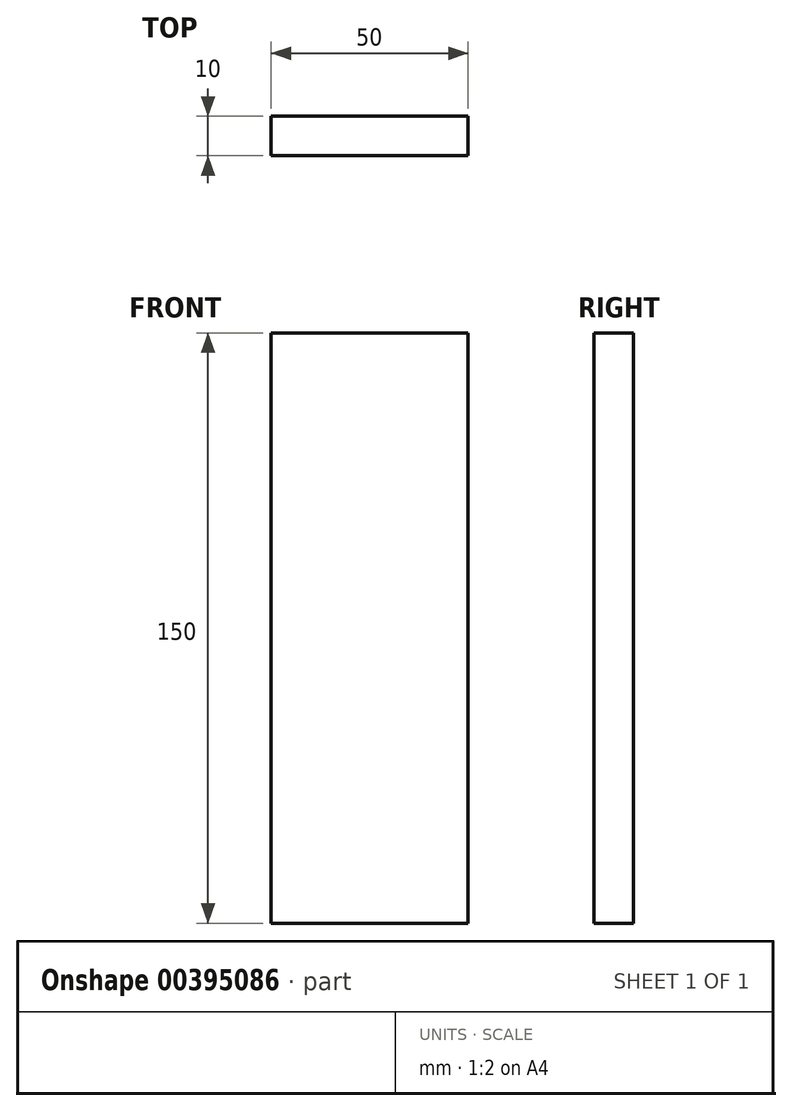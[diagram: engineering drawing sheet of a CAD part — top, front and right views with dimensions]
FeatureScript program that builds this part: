
annotation { "Feature Type Name" : "Feature", "Feature Type Description" : "" }
export const myFeature = defineFeature(function(context is Context, id is Id, definition is map)
    precondition{}
    {
        {
            var Q0;
            Q0=qCreatedBy(makeId("Front.planeOp"),FACE);
            var sketch = newSketch(context, id + "F0", { "sketchPlane" : qUnion([Q0])});
            skLineSegment(sketch, "E0.bottom", {"start": v(-25, -75) * mm, "end": v(25, -75) * mm});
            skLineSegment(sketch, "E0.top", {"start": v(-25, 75) * mm, "end": v(25, 75) * mm});
            skLineSegment(sketch, "E0.left", {"start": v(-25, -75) * mm, "end": v(-25, 75) * mm});
            skLineSegment(sketch, "E0.right", {"start": v(25, -75) * mm, "end": v(25, 75) * mm});
            skPoint(sketch, "E0.middle", {"position": v(0, 0) * mm});
            skSolve(sketch);
        }
        {
            var Q0;
            Q0 = qSketchRegion(id + "F0", true);
            extrude(context, id + "F1", {"entities" : qUnion([Q0]), "depth" : 10 * mm});
        }
    });
